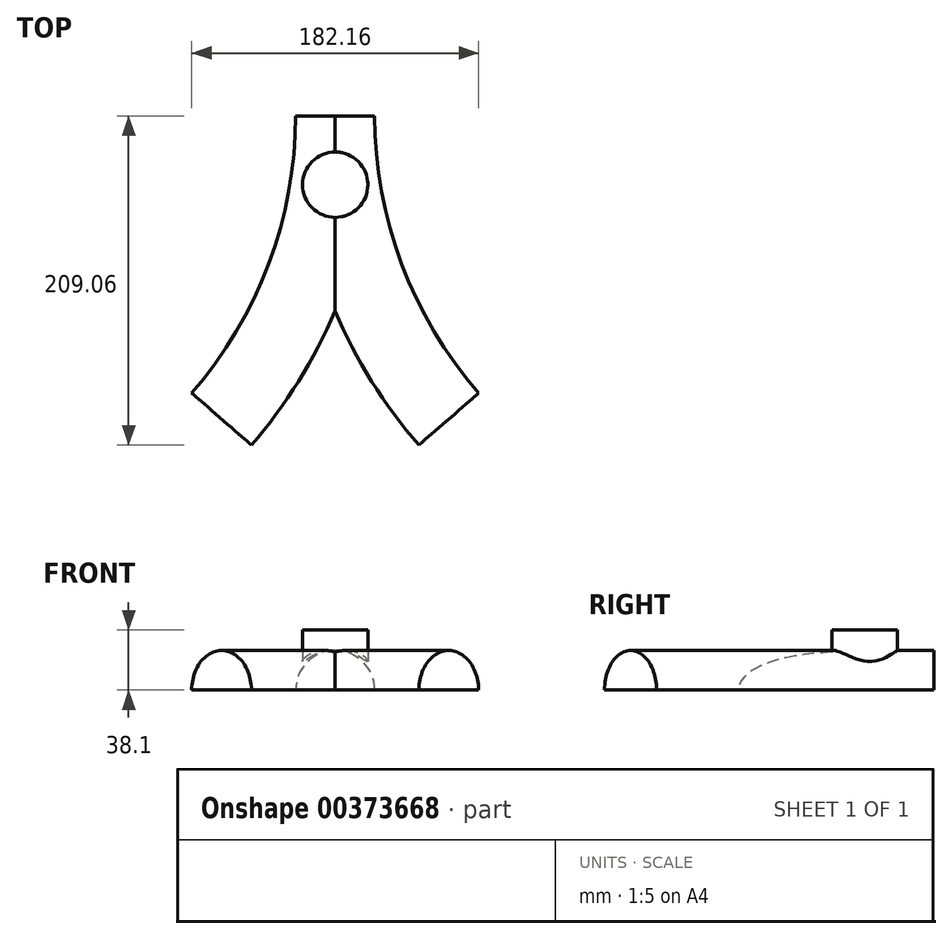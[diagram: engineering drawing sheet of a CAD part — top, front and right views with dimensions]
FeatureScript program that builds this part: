
annotation { "Feature Type Name" : "Feature", "Feature Type Description" : "" }
export const myFeature = defineFeature(function(context is Context, id is Id, definition is map)
    precondition{}
    {
        {
            var Q0;
            Q0=qCreatedBy(makeId("Top.planeOp"),FACE);
            var sketch = newSketch(context, id + "F0", { "sketchPlane" : qUnion([Q0])});
            skLineSegment(sketch, "E0", {"start": v(0, 0) * mm, "end": v(0, -43.68) * mm});
            skCircle(sketch, "E1", {"center": v(0, -43.68) * mm, "radius": 20.77 * mm});
            skSolve(sketch);
        }
        {
            var Q0;
            {var subQ0=sQuery(id+"F0.wireOp",EDGE,"E1");Q0=makeQuery(id+"F0.imprint","IMPRINT",FACE,{"disambiguationData":[TD([[makeQuery(id+"F0.imprint","IMPRINT",EDGE,{"derivedFrom":subQ0}),1.0]])]});}
            extrude(context, id + "F1", {"entities" : qUnion([Q0]), "depth" : 38.1 * mm});
        }
        {
            var Q0;
            Q0=qCreatedBy(makeId("Top.planeOp"),FACE);
            var sketch = newSketch(context, id + "F2", { "sketchPlane" : qUnion([Q0])});
            skArc(sketch, "E2", {"start": v(-72.14, -192.55) * mm, "mid": v(-18.63, -102.8) * mm, "end": v(0, 0) * mm});
            skLineSegment(sketch, "E3", {"start": v(0, 0) * mm, "end": v(0, -167.15) * mm, "construction": true});
            skArc(sketch, "E4.MirrorCS", {"start": v(72.14, -192.55) * mm, "mid": v(18.63, -102.8) * mm, "end": v(0, 0) * mm});
            skSolve(sketch);
        }
        {
            var Q0;
            Q0=qCreatedBy(makeId("Front.planeOp"),FACE);
            var sketch = newSketch(context, id + "F3", { "sketchPlane" : qUnion([Q0])});
            skLineSegment(sketch, "E5", {"start": v(25.13, 0) * mm, "end": v(-25.13, 0) * mm});
            skArc(sketch, "E6", {"start": v(25.13, 0) * mm, "mid": v(0, 25.13) * mm, "end": v(-25.13, 0) * mm});
            skSolve(sketch);
        }
        {
            var Q0;
            Q0=makeQuery(id+"F3.imprint","IMPRINT",FACE,{"disambiguationData":[TD([[makeQuery(id+"F3.imprint","IMPRINT",EDGE,{"derivedFrom":sQuery(id+"F3.wireOp",EDGE,"E5")}),-1.0]])]});
            var Q1;
            Q1=sQuery(id+"F2.wireOp",EDGE,"E2");
            sweep(context, id + "F4", {"operationType" : NewBodyOperationType.ADD, "profiles" : qUnion([Q0]), "path" : qUnion([Q1])});
        }
        {
            var Q0;
            Q0=makeQuery(id+"F4.opSweep","CAP_FACE",FACE,{"disambiguationData":[OSD([sQuery(id+"F2.wireOp",VERTEX,"E2.end"),sQuery(id+"F3.wireOp",EDGE,"E5"),sQuery(id+"F3.wireOp",EDGE,"E6")])],"isStart":true});
            var Q1;
            Q1=sQuery(id+"F2.wireOp",EDGE,"E4.MirrorCS");
            sweep(context, id + "F5", {"operationType" : NewBodyOperationType.ADD, "profiles" : qUnion([Q0]), "path" : qUnion([Q1])});
        }
    });
